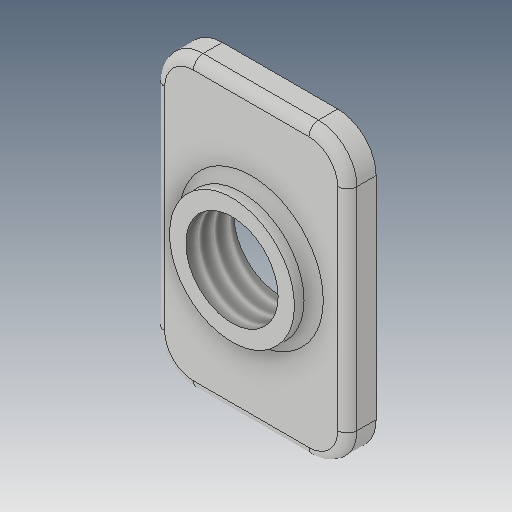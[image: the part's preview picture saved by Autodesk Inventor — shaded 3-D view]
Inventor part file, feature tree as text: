
AUTODESK INVENTOR PART (.ipt)
format: ipt  version: 2017 (Build 210142000, 142)  size: 165,376 bytes
history: native  units: mm
features: other x3, sketch x2
ambient origin geometry x8: Origin, YZ Plane, XZ Plane, XY Plane, X Axis, Y Axis, Z Axis, Center Point
bodies: Solid1 (feature_tree)
feature tree (5):
  other  "M5 Tee Nut_MIR.ipt"
  other  "Solid1::M5 Tee Nut_MIR.ipt"
  other  "TaggingFeature1"
  sketch  "Sketch1"  dims[d0=10.0mm]
  sketch  "Sketch2"
